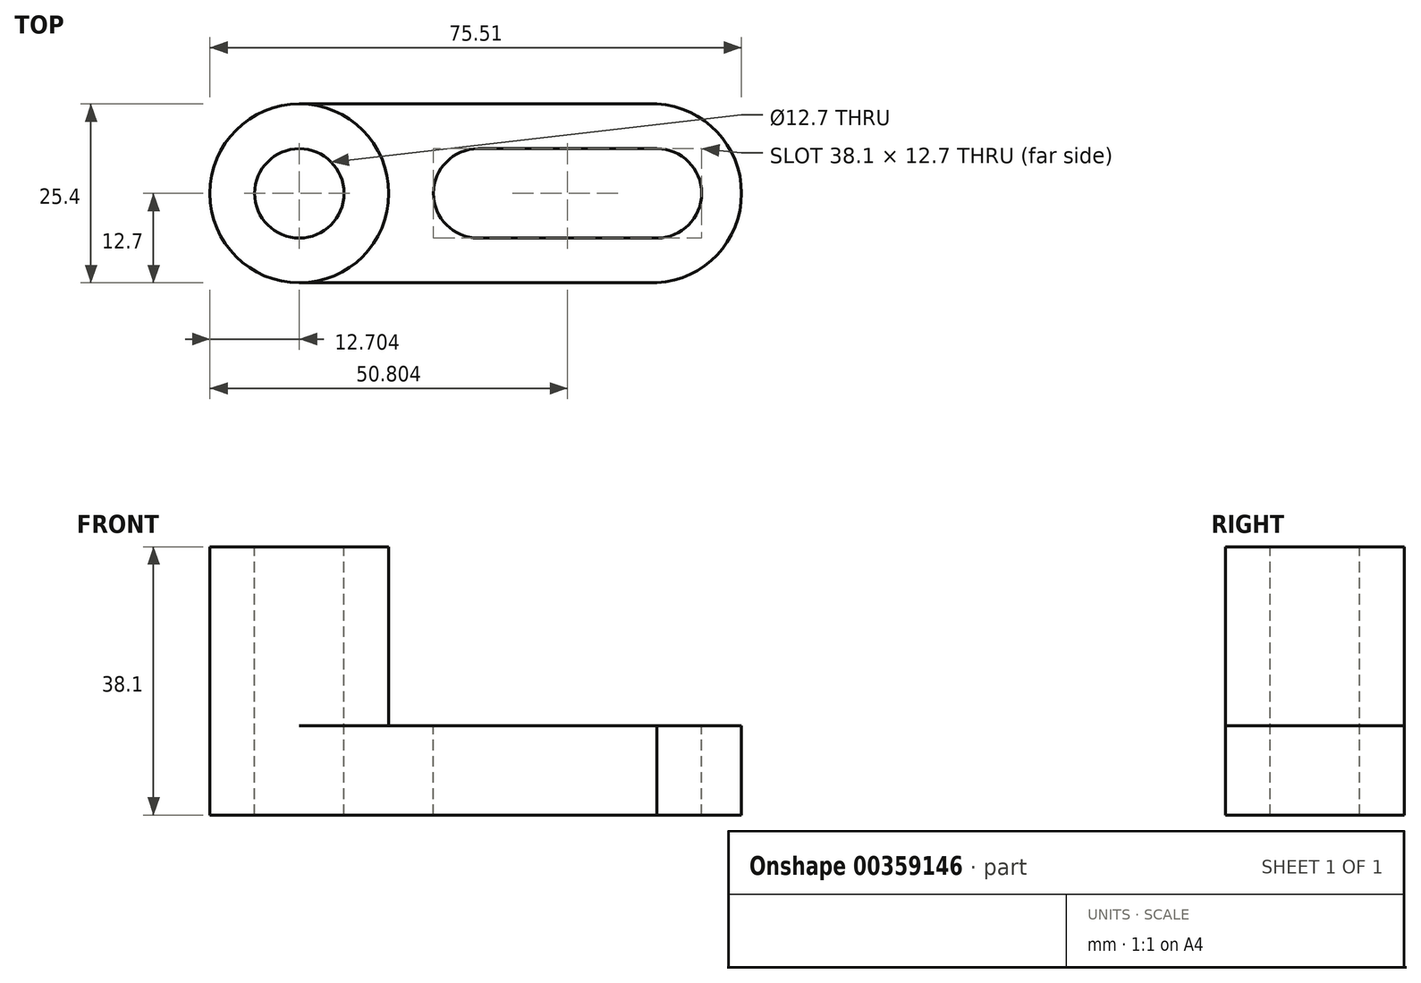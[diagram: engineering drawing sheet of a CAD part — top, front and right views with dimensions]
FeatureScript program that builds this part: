
annotation { "Feature Type Name" : "Feature", "Feature Type Description" : "" }
export const myFeature = defineFeature(function(context is Context, id is Id, definition is map)
    precondition{}
    {
        {
            var Q0;
            Q0=qCreatedBy(makeId("Front.planeOp"),FACE);
            var sketch = newSketch(context, id + "F0", { "sketchPlane" : qUnion([Q0])});
            skLineSegment(sketch, "E0", {"start": v(-47.69, 16.83) * mm, "end": v(-47.69, 4.13) * mm});
            skLineSegment(sketch, "E1", {"start": v(-47.69, 4.13) * mm, "end": v(28.51, 4.13) * mm});
            skLineSegment(sketch, "E2", {"start": v(28.51, 4.13) * mm, "end": v(28.51, 16.83) * mm});
            skLineSegment(sketch, "E3", {"start": v(28.51, 16.83) * mm, "end": v(-47.69, 16.83) * mm});
            skSolve(sketch);
        }
        {
            var Q0;
            Q0 = qSketchRegion(id + "F0", true);
            extrude(context, id + "F1", {"entities" : qUnion([Q0]), "depth" : 25.4 * mm});
        }
        {
            var Q0;
            Q0=makeQuery(id+"F1.opExtrude","SWEPT_FACE",FACE,{"disambiguationData":[OSD([sQuery(id+"F0.wireOp",EDGE,"E3")])]});
            var sketch = newSketch(context, id + "F2", { "sketchPlane" : qUnion([Q0])});
            skCircle(sketch, "E4", {"center": v(-34.99, -12.7) * mm, "radius": 12.7 * mm});
            skSolve(sketch);
        }
        {
            var Q0;
            Q0 = qSketchRegion(id + "F2", true);
            extrude(context, id + "F3", {"entities" : qUnion([Q0]), "operationType" : NewBodyOperationType.ADD, "depth" : 25.4 * mm});
        }
        {
            var Q0;
            {var subQ0=sQuery(id+"F0.wireOp",EDGE,"E0");var subQ1=sQuery(id+"F0.wireOp",EDGE,"E3");var subQ2=makeQuery(id+"F1.opExtrude","SWEPT_FACE",FACE,{"disambiguationData":[OSD([subQ1])]});Q0=makeQuery(id+"F3.boolean.opBoolean","SPLIT",FACE,{"disambiguationData":[TD([makeQuery(id+"F1.opExtrude","SWEPT_FACE",FACE,{"disambiguationData":[OSD([subQ0])]}),makeQuery(id+"F1.opExtrude","CAP_FACE",FACE,{"disambiguationData":[OSD([subQ0,sQuery(id+"F0.wireOp",EDGE,"E1"),sQuery(id+"F0.wireOp",EDGE,"E2"),subQ1])],"isStart":true}),subQ2,makeQuery(id+"F3.opExtrude","SWEPT_FACE",FACE,{"disambiguationData":[OSD([sQuery(id+"F2.wireOp",EDGE,"E4")])]})])],"derivedFrom":subQ2});}
            var Q1;
            {var subQ0=sQuery(id+"F0.wireOp",EDGE,"E0");var subQ1=sQuery(id+"F0.wireOp",EDGE,"E3");var subQ2=makeQuery(id+"F1.opExtrude","SWEPT_FACE",FACE,{"disambiguationData":[OSD([subQ1])]});Q1=makeQuery(id+"F3.boolean.opBoolean","SPLIT",FACE,{"disambiguationData":[TD([makeQuery(id+"F1.opExtrude","SWEPT_FACE",FACE,{"disambiguationData":[OSD([subQ0])]}),makeQuery(id+"F1.opExtrude","CAP_FACE",FACE,{"disambiguationData":[OSD([subQ0,sQuery(id+"F0.wireOp",EDGE,"E1"),sQuery(id+"F0.wireOp",EDGE,"E2"),subQ1])],"isStart":false}),subQ2,makeQuery(id+"F3.opExtrude","SWEPT_FACE",FACE,{"disambiguationData":[OSD([sQuery(id+"F2.wireOp",EDGE,"E4")])]})])],"derivedFrom":subQ2});}
            extrude(context, id + "F4", {"entities" : qUnion([Q0, Q1]), "operationType" : NewBodyOperationType.REMOVE, "oppositeDirection" : true, "depth" : 12.7 * mm});
        }
        {
            var Q0;
            Q0=makeQuery(id+"F3.opExtrude","CAP_FACE",FACE,{"disambiguationData":[OSD([sQuery(id+"F2.wireOp",EDGE,"E4")])],"isStart":false});
            var sketch = newSketch(context, id + "F5", { "sketchPlane" : qUnion([Q0])});
            skCircle(sketch, "E5", {"center": v(-34.99, -12.7) * mm, "radius": 6.35 * mm});
            skSolve(sketch);
        }
        {
            var Q0;
            Q0 = qSketchRegion(id + "F5", true);
            extrude(context, id + "F6", {"entities" : qUnion([Q0]), "operationType" : NewBodyOperationType.REMOVE, "oppositeDirection" : true, "depth" : 38.1 * mm});
        }
        {
            var Q0;
            {var subQ0=sQuery(id+"F0.wireOp",EDGE,"E3");var subQ1=makeQuery(id+"F1.opExtrude","SWEPT_FACE",FACE,{"disambiguationData":[OSD([subQ0])]});var subQ2=sQuery(id+"F0.wireOp",EDGE,"E2");var subQ3=sQuery(id+"F0.wireOp",EDGE,"E1");var subQ4=sQuery(id+"F0.wireOp",EDGE,"E0");Q0=makeQuery(id+"F3.boolean.opBoolean","SPLIT",FACE,{"disambiguationData":[TD([makeQuery(id+"F1.opExtrude","CAP_FACE",FACE,{"disambiguationData":[OSD([subQ4,subQ3,subQ2,subQ0])],"isStart":true}),makeQuery(id+"F1.opExtrude","CAP_FACE",FACE,{"disambiguationData":[OSD([subQ4,subQ3,subQ2,subQ0])],"isStart":false}),makeQuery(id+"F1.opExtrude","SWEPT_FACE",FACE,{"disambiguationData":[OSD([subQ2])]}),subQ1,makeQuery(id+"F3.opExtrude","SWEPT_FACE",FACE,{"disambiguationData":[OSD([sQuery(id+"F2.wireOp",EDGE,"E4")])]})])],"derivedFrom":subQ1});}
            var sketch = newSketch(context, id + "F7", { "sketchPlane" : qUnion([Q0])});
            skCircle(sketch, "E6", {"center": v(-9.59, -12.7) * mm, "radius": 6.35 * mm});
            skCircle(sketch, "E7", {"center": v(15.81, -12.7) * mm, "radius": 6.35 * mm});
            skLineSegment(sketch, "E8", {"start": v(-9.59, -6.35) * mm, "end": v(15.81, -6.35) * mm});
            skLineSegment(sketch, "E9", {"start": v(-9.59, -19.05) * mm, "end": v(15.81, -19.05) * mm});
            skArc(sketch, "E10", {"start": v(15.81, -25.4) * mm, "mid": v(27.82, -12.7) * mm, "end": v(15.81, 0) * mm});
            skSolve(sketch);
        }
        {
            var Q0;
            Q0 = qSketchRegion(id + "F7", true);
            var Q1;
            {var subQ0=sQuery(id+"F7.wireOp",EDGE,"E10");Q1=makeQuery(id+"F7.imprint","IMPRINT",FACE,{"disambiguationData":[TD([[makeQuery(id+"F7.imprint","IMPRINT",EDGE,{"derivedFrom":subQ0}),-1.0]])]});}
            extrude(context, id + "F8", {"entities" : qUnion([Q0, Q1]), "operationType" : NewBodyOperationType.REMOVE, "oppositeDirection" : true, "depth" : 12.7 * mm});
        }
    });
